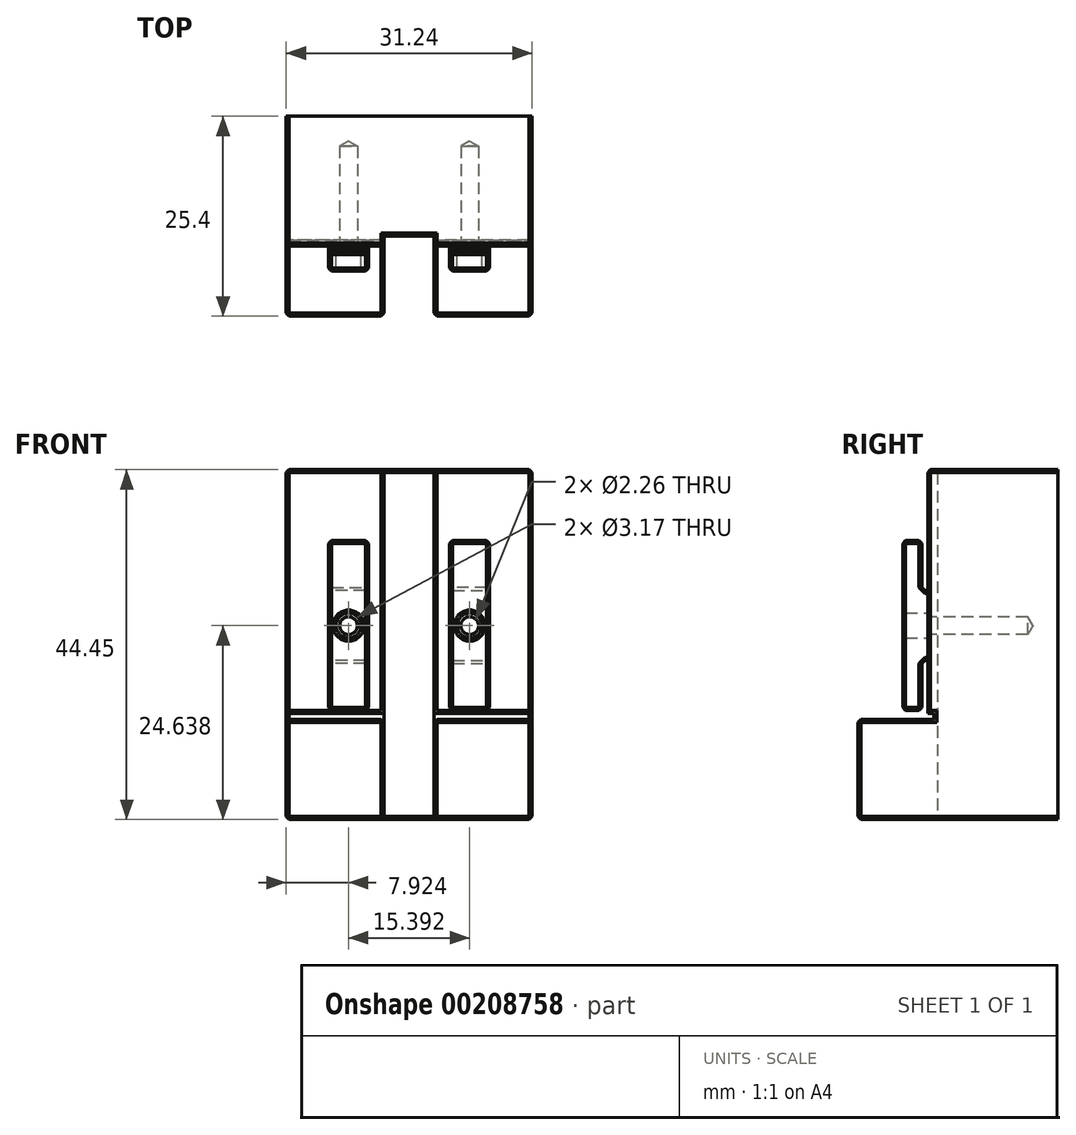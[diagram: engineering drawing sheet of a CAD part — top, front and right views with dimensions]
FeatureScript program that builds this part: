
annotation { "Feature Type Name" : "Feature", "Feature Type Description" : "" }
export const myFeature = defineFeature(function(context is Context, id is Id, definition is map)
    precondition{}
    {
        {
            var Q0;
            Q0=qCreatedBy(makeId("Top.planeOp"),FACE);
            var sketch = newSketch(context, id + "F0", { "sketchPlane" : qUnion([Q0])});
            skLineSegment(sketch, "E0.bottom", {"start": v(15.62, 19.05) * mm, "end": v(3.18, 19.05) * mm});
            skLineSegment(sketch, "E0.top", {"start": v(15.62, -19.05) * mm, "end": v(3.17, -19.05) * mm});
            skLineSegment(sketch, "E0.left", {"start": v(15.62, 19.05) * mm, "end": v(15.62, -19.05) * mm});
            skLineSegment(sketch, "E0.right", {"start": v(-15.62, 19.05) * mm, "end": v(-15.62, -19.05) * mm});
            skPoint(sketch, "E0.middle", {"position": v(0, 0) * mm});
            skLineSegment(sketch, "E1.0", {"start": v(-3.17, 19.05) * mm, "end": v(-3.18, 8.89) * mm});
            skLineSegment(sketch, "E2.0", {"start": v(3.18, 19.05) * mm, "end": v(3.18, 8.89) * mm});
            skLineSegment(sketch, "E3.0", {"start": v(3.18, -8.89) * mm, "end": v(-3.18, -8.89) * mm});
            skLineSegment(sketch, "E4.0", {"start": v(3.18, 8.89) * mm, "end": v(-3.18, 8.89) * mm});
            skLineSegment(sketch, "E5.trimOffspring", {"start": v(-3.18, 19.05) * mm, "end": v(-15.62, 19.05) * mm});
            skLineSegment(sketch, "E6.trimOffspring", {"start": v(-3.18, -8.89) * mm, "end": v(-3.18, -19.05) * mm});
            skLineSegment(sketch, "E7.trimOffspring", {"start": v(3.18, -8.89) * mm, "end": v(3.17, -19.05) * mm});
            skLineSegment(sketch, "E8.trimOffspring", {"start": v(-3.18, -19.05) * mm, "end": v(-15.62, -19.05) * mm});
            skSolve(sketch);
        }
        {
            var Q0;
            Q0=makeQuery(id+"F0.imprint","IMPRINT",FACE,{"disambiguationData":[TD([[makeQuery(id+"F0.imprint","IMPRINT",EDGE,{"derivedFrom":sQuery(id+"F0.wireOp",EDGE,"E0.bottom")}),1.0]])]});
            extrude(context, id + "F1", {"entities" : qUnion([Q0]), "depth" : 44.45 * mm});
        }
        {
            var Q0;
            Q0=makeQuery(id+"F1.opExtrude","CAP_FACE",FACE,{"disambiguationData":[OSD([sQuery(id+"F0.wireOp",EDGE,"E0.bottom"),sQuery(id+"F0.wireOp",EDGE,"E0.top"),sQuery(id+"F0.wireOp",EDGE,"E0.left"),sQuery(id+"F0.wireOp",EDGE,"E0.right"),sQuery(id+"F0.wireOp",EDGE,"E1.0"),sQuery(id+"F0.wireOp",EDGE,"E2.0"),sQuery(id+"F0.wireOp",EDGE,"E3.0"),sQuery(id+"F0.wireOp",EDGE,"E4.0"),sQuery(id+"F0.wireOp",EDGE,"E5.trimOffspring"),sQuery(id+"F0.wireOp",EDGE,"E6.trimOffspring"),sQuery(id+"F0.wireOp",EDGE,"E7.trimOffspring"),sQuery(id+"F0.wireOp",EDGE,"E8.trimOffspring")])],"isStart":false});
            var sketch = newSketch(context, id + "F2", { "sketchPlane" : qUnion([Q0])});
            skLineSegment(sketch, "E9.bottom", {"start": v(-15.62, -19.05) * mm, "end": v(15.62, -19.05) * mm});
            skLineSegment(sketch, "E9.top", {"start": v(-15.62, -10.16) * mm, "end": v(15.62, -10.16) * mm});
            skLineSegment(sketch, "E9.left", {"start": v(-15.62, -19.05) * mm, "end": v(-15.62, -10.16) * mm});
            skLineSegment(sketch, "E9.right", {"start": v(15.62, -19.05) * mm, "end": v(15.62, -10.16) * mm});
            skLineSegment(sketch, "E10.MirrorCS", {"start": v(-15.62, 10.16) * mm, "end": v(15.62, 10.16) * mm});
            skLineSegment(sketch, "E11.MirrorCS", {"start": v(-15.62, 19.05) * mm, "end": v(-15.62, 10.16) * mm});
            skLineSegment(sketch, "E12.MirrorCS", {"start": v(-15.62, 19.05) * mm, "end": v(15.62, 19.05) * mm});
            skLineSegment(sketch, "E13.MirrorCS", {"start": v(15.62, 19.05) * mm, "end": v(15.62, 10.16) * mm});
            skSolve(sketch);
        }
        {
            var Q0;
            {var subQ0=sQuery(id+"F2.wireOp",EDGE,"E9.left");Q0=makeQuery(id+"F2.imprint","IMPRINT",FACE,{"disambiguationData":[TD([[makeQuery(id+"F2.imprint","IMPRINT",EDGE,{"derivedFrom":subQ0}),1.0]])]});}
            var Q1;
            {var subQ0=sQuery(id+"F2.wireOp",EDGE,"E9.right");Q1=makeQuery(id+"F2.imprint","IMPRINT",FACE,{"disambiguationData":[TD([[makeQuery(id+"F2.imprint","IMPRINT",EDGE,{"derivedFrom":subQ0}),-1.0]])]});}
            var Q2;
            {var subQ0=sQuery(id+"F2.wireOp",EDGE,"E13.MirrorCS");Q2=makeQuery(id+"F2.imprint","IMPRINT",FACE,{"disambiguationData":[TD([[makeQuery(id+"F2.imprint","IMPRINT",EDGE,{"derivedFrom":subQ0}),-1.0]])]});}
            var Q3;
            {var subQ0=sQuery(id+"F2.wireOp",EDGE,"E11.MirrorCS");Q3=makeQuery(id+"F2.imprint","IMPRINT",FACE,{"disambiguationData":[TD([[makeQuery(id+"F2.imprint","IMPRINT",EDGE,{"derivedFrom":subQ0}),1.0]])]});}
            extrude(context, id + "F3", {"entities" : qUnion([Q0, Q1, Q2, Q3]), "operationType" : NewBodyOperationType.REMOVE, "oppositeDirection" : true, "depth" : 31.75 * mm});
        }
        {
            var Q0;
            Q0=makeQuery(id+"F1.opExtrude","SWEPT_FACE",FACE,{"disambiguationData":[OSD([sQuery(id+"F0.wireOp",EDGE,"E0.left")])]});
            var sketch = newSketch(context, id + "F4", { "sketchPlane" : qUnion([Q0])});
            skLineSegment(sketch, "E14.bottom", {"start": v(-10.16, 12.7) * mm, "end": v(-9.37, 12.7) * mm});
            skLineSegment(sketch, "E14.top", {"start": v(-10.16, 13.49) * mm, "end": v(-9.37, 13.49) * mm});
            skLineSegment(sketch, "E14.left", {"start": v(-10.16, 12.7) * mm, "end": v(-10.16, 13.49) * mm});
            skLineSegment(sketch, "E14.right", {"start": v(-9.37, 12.7) * mm, "end": v(-9.37, 13.49) * mm});
            skLineSegment(sketch, "E15.MirrorCS", {"start": v(10.16, 13.49) * mm, "end": v(9.37, 13.49) * mm});
            skLineSegment(sketch, "E16.MirrorCS", {"start": v(9.37, 12.7) * mm, "end": v(9.37, 13.49) * mm});
            skLineSegment(sketch, "E17.MirrorCS", {"start": v(10.16, 12.7) * mm, "end": v(9.37, 12.7) * mm});
            skLineSegment(sketch, "E18.MirrorCS", {"start": v(10.16, 12.7) * mm, "end": v(10.16, 13.49) * mm});
            skSolve(sketch);
        }
        {
            var Q0;
            Q0=makeQuery(id+"F4.imprint","IMPRINT",FACE,{"disambiguationData":[TD([[makeQuery(id+"F4.imprint","IMPRINT",EDGE,{"derivedFrom":sQuery(id+"F4.wireOp",EDGE,"E14.bottom")}),1.0]])]});
            var Q1;
            Q1=makeQuery(id+"F4.imprint","IMPRINT",FACE,{"disambiguationData":[TD([[makeQuery(id+"F4.imprint","IMPRINT",EDGE,{"derivedFrom":sQuery(id+"F4.wireOp",EDGE,"E15.MirrorCS")}),1.0]])]});
            extrude(context, id + "F5", {"entities" : qUnion([Q0, Q1]), "operationType" : NewBodyOperationType.REMOVE, "endBound" : BoundingType.THROUGH_ALL, "oppositeDirection" : true, "depth" : 25.4 * mm});
        }
        {
            var Q0;
            {var subQ0=sQuery(id+"F2.wireOp",EDGE,"E10.MirrorCS");Q0=makeQuery(id+"F3.boolean.opBoolean","COPY",FACE,{"derivedFrom":makeQuery(id+"F3.opExtrude","SWEPT_FACE",FACE,{"disambiguationData":[OSD([subQ0]),TDD([makeQuery(id+"F2.imprint","IMPRINT",EDGE,{"disambiguationData":[TD([[makeQuery(id+"F2.imprint","INTERSECT",VERTEX,{"derivedFrom":[makeQuery(id+"F1.opExtrude","CAP_EDGE",EDGE,{"disambiguationData":[OSD([sQuery(id+"F0.wireOp",EDGE,"E2.0")])],"isStart":false}),subQ0]}),-1.0]])],"derivedFrom":subQ0})])]})});}
            var Q1;
            {var subQ0=sQuery(id+"F2.wireOp",EDGE,"E10.MirrorCS");Q1=makeQuery(id+"F3.boolean.opBoolean","COPY",FACE,{"derivedFrom":makeQuery(id+"F3.opExtrude","SWEPT_FACE",FACE,{"disambiguationData":[OSD([subQ0]),TDD([makeQuery(id+"F2.imprint","IMPRINT",EDGE,{"disambiguationData":[TD([[makeQuery(id+"F2.imprint","INTERSECT",VERTEX,{"derivedFrom":[makeQuery(id+"F1.opExtrude","CAP_EDGE",EDGE,{"disambiguationData":[OSD([sQuery(id+"F0.wireOp",EDGE,"E1.0")])],"isStart":false}),subQ0]}),1.0]])],"derivedFrom":subQ0})])]})});}
            var Q2;
            Q2=makeQuery(id+"F1.opExtrude","SWEPT_FACE",FACE,{"disambiguationData":[OSD([sQuery(id+"F0.wireOp",EDGE,"E5.trimOffspring")])]});
            var Q3;
            Q3=makeQuery(id+"F1.opExtrude","SWEPT_FACE",FACE,{"disambiguationData":[OSD([sQuery(id+"F0.wireOp",EDGE,"E0.bottom")])]});
            var Q4;
            Q4=makeQuery(id+"F1.opExtrude","SWEPT_FACE",FACE,{"disambiguationData":[OSD([sQuery(id+"F0.wireOp",EDGE,"E0.right")])]});
            var Q5;
            {var subQ0=sQuery(id+"F2.wireOp",EDGE,"E9.top");Q5=makeQuery(id+"F3.boolean.opBoolean","COPY",FACE,{"derivedFrom":makeQuery(id+"F3.opExtrude","SWEPT_FACE",FACE,{"disambiguationData":[OSD([subQ0]),TDD([makeQuery(id+"F2.imprint","IMPRINT",EDGE,{"disambiguationData":[TD([[makeQuery(id+"F2.imprint","INTERSECT",VERTEX,{"derivedFrom":[makeQuery(id+"F1.opExtrude","CAP_EDGE",EDGE,{"disambiguationData":[OSD([sQuery(id+"F0.wireOp",EDGE,"E7.trimOffspring")])],"isStart":false}),subQ0]}),-1.0]])],"derivedFrom":subQ0})])]})});}
            var Q6;
            Q6=makeQuery(id+"F1.opExtrude","SWEPT_FACE",FACE,{"disambiguationData":[OSD([sQuery(id+"F0.wireOp",EDGE,"E0.top")])]});
            var Q7;
            Q7=makeQuery(id+"F1.opExtrude","SWEPT_FACE",FACE,{"disambiguationData":[OSD([sQuery(id+"F0.wireOp",EDGE,"E8.trimOffspring")])]});
            var Q8;
            Q8=makeQuery(id+"F1.opExtrude","CAP_FACE",FACE,{"disambiguationData":[OSD([sQuery(id+"F0.wireOp",EDGE,"E0.bottom"),sQuery(id+"F0.wireOp",EDGE,"E0.top"),sQuery(id+"F0.wireOp",EDGE,"E0.left"),sQuery(id+"F0.wireOp",EDGE,"E0.right"),sQuery(id+"F0.wireOp",EDGE,"E1.0"),sQuery(id+"F0.wireOp",EDGE,"E2.0"),sQuery(id+"F0.wireOp",EDGE,"E3.0"),sQuery(id+"F0.wireOp",EDGE,"E4.0"),sQuery(id+"F0.wireOp",EDGE,"E5.trimOffspring"),sQuery(id+"F0.wireOp",EDGE,"E6.trimOffspring"),sQuery(id+"F0.wireOp",EDGE,"E7.trimOffspring"),sQuery(id+"F0.wireOp",EDGE,"E8.trimOffspring")])],"isStart":true});
            var Q9;
            Q9=makeQuery(id+"F1.opExtrude","CAP_FACE",FACE,{"disambiguationData":[OSD([sQuery(id+"F0.wireOp",EDGE,"E0.bottom"),sQuery(id+"F0.wireOp",EDGE,"E0.top"),sQuery(id+"F0.wireOp",EDGE,"E0.left"),sQuery(id+"F0.wireOp",EDGE,"E0.right"),sQuery(id+"F0.wireOp",EDGE,"E1.0"),sQuery(id+"F0.wireOp",EDGE,"E2.0"),sQuery(id+"F0.wireOp",EDGE,"E3.0"),sQuery(id+"F0.wireOp",EDGE,"E4.0"),sQuery(id+"F0.wireOp",EDGE,"E5.trimOffspring"),sQuery(id+"F0.wireOp",EDGE,"E6.trimOffspring"),sQuery(id+"F0.wireOp",EDGE,"E7.trimOffspring"),sQuery(id+"F0.wireOp",EDGE,"E8.trimOffspring")])],"isStart":false});
            var Q10;
            Q10=makeQuery(id+"F5.boolean.opBoolean","INTERSECT",EDGE,{"derivedFrom":[makeQuery(id+"F1.opExtrude","SWEPT_FACE",FACE,{"disambiguationData":[OSD([sQuery(id+"F0.wireOp",EDGE,"E6.trimOffspring")])]}),makeQuery(id+"F5.opExtrude","SWEPT_FACE",FACE,{"disambiguationData":[OSD([sQuery(id+"F4.wireOp",EDGE,"E14.bottom")])]})]});
            var Q11;
            Q11=makeQuery(id+"F5.boolean.opBoolean","INTERSECT",EDGE,{"derivedFrom":[makeQuery(id+"F1.opExtrude","SWEPT_FACE",FACE,{"disambiguationData":[OSD([sQuery(id+"F0.wireOp",EDGE,"E7.trimOffspring")])]}),makeQuery(id+"F5.opExtrude","SWEPT_FACE",FACE,{"disambiguationData":[OSD([sQuery(id+"F4.wireOp",EDGE,"E14.bottom")])]})]});
            var Q12;
            Q12=makeQuery(id+"F5.boolean.opBoolean","INTERSECT",EDGE,{"derivedFrom":[makeQuery(id+"F1.opExtrude","SWEPT_FACE",FACE,{"disambiguationData":[OSD([sQuery(id+"F0.wireOp",EDGE,"E2.0")])]}),makeQuery(id+"F5.opExtrude","SWEPT_FACE",FACE,{"disambiguationData":[OSD([sQuery(id+"F4.wireOp",EDGE,"E17.MirrorCS")])]})]});
            var Q13;
            Q13=makeQuery(id+"F5.boolean.opBoolean","INTERSECT",EDGE,{"derivedFrom":[makeQuery(id+"F1.opExtrude","SWEPT_FACE",FACE,{"disambiguationData":[OSD([sQuery(id+"F0.wireOp",EDGE,"E1.0")])]}),makeQuery(id+"F5.opExtrude","SWEPT_FACE",FACE,{"disambiguationData":[OSD([sQuery(id+"F4.wireOp",EDGE,"E17.MirrorCS")])]})]});
            var Q14;
            Q14=makeQuery(id+"F5.boolean.opBoolean","MERGE",EDGE,{"derivedFrom":[makeQuery(id+"F3.boolean.opBoolean","COPY",EDGE,{"derivedFrom":makeQuery(id+"F3.opExtrude","CAP_EDGE",EDGE,{"disambiguationData":[OSD([sQuery(id+"F2.wireOp",EDGE,"E9.right")])],"isStart":false})}),makeQuery(id+"F5.opExtrude","CAP_EDGE",EDGE,{"disambiguationData":[OSD([sQuery(id+"F4.wireOp",EDGE,"E14.bottom")])],"isStart":true})]});
            var Q15;
            Q15=makeQuery(id+"F3.boolean.opBoolean","COPY",EDGE,{"derivedFrom":makeQuery(id+"F3.opExtrude","SWEPT_EDGE",EDGE,{"disambiguationData":[OSD([sQuery(id+"F0.wireOp",EDGE,"E6.trimOffspring"),sQuery(id+"F2.wireOp",EDGE,"E9.top")])]})});
            var Q16;
            Q16=makeQuery(id+"F5.boolean.opBoolean","MERGE",EDGE,{"derivedFrom":[makeQuery(id+"F3.boolean.opBoolean","COPY",EDGE,{"derivedFrom":makeQuery(id+"F3.opExtrude","CAP_EDGE",EDGE,{"disambiguationData":[OSD([sQuery(id+"F2.wireOp",EDGE,"E13.MirrorCS")])],"isStart":false})}),makeQuery(id+"F5.opExtrude","CAP_EDGE",EDGE,{"disambiguationData":[OSD([sQuery(id+"F4.wireOp",EDGE,"E17.MirrorCS")])],"isStart":true})]});
            chamfer(context, id + "F6", {"entities" : qUnion([Q0, Q1, Q2, Q3, Q4, Q5, Q6, Q7, Q8, Q9, Q10, Q11, Q12, Q13, Q14, Q15, Q16]), "width" : 0.38 * mm, "tangentPropagation" : true});
        }
        {
            var Q0;
            {var subQ0=sQuery(id+"F2.wireOp",EDGE,"E9.top");Q0=makeQuery(id+"F3.boolean.opBoolean","COPY",FACE,{"derivedFrom":makeQuery(id+"F3.opExtrude","SWEPT_FACE",FACE,{"disambiguationData":[OSD([subQ0]),TDD([makeQuery(id+"F2.imprint","IMPRINT",EDGE,{"disambiguationData":[TD([[makeQuery(id+"F2.imprint","INTERSECT",VERTEX,{"derivedFrom":[makeQuery(id+"F1.opExtrude","CAP_EDGE",EDGE,{"disambiguationData":[OSD([sQuery(id+"F0.wireOp",EDGE,"E7.trimOffspring")])],"isStart":false}),subQ0]}),-1.0]])],"derivedFrom":subQ0})])]})});}
            var sketch = newSketch(context, id + "F7", { "sketchPlane" : qUnion([Q0])});
            skCircle(sketch, "E19", {"center": v(7.7, 24.64) * mm, "radius": 1.42 * mm});
            skSolve(sketch);
        }
        {
            var Q0;
            Q0=sQuery(id+"F7.wireOp",VERTEX,"E19.center");
            var Q1;
            Q1=makeQuery(id+"F1.opExtrude","SWEPT_BODY",BODY,{"disambiguationData":[OSD([sQuery(id+"F0.wireOp",EDGE,"E0.bottom"),sQuery(id+"F0.wireOp",EDGE,"E0.top"),sQuery(id+"F0.wireOp",EDGE,"E0.left"),sQuery(id+"F0.wireOp",EDGE,"E0.right"),sQuery(id+"F0.wireOp",EDGE,"E1.0"),sQuery(id+"F0.wireOp",EDGE,"E2.0"),sQuery(id+"F0.wireOp",EDGE,"E3.0"),sQuery(id+"F0.wireOp",EDGE,"E4.0"),sQuery(id+"F0.wireOp",EDGE,"E5.trimOffspring"),sQuery(id+"F0.wireOp",EDGE,"E6.trimOffspring"),sQuery(id+"F0.wireOp",EDGE,"E7.trimOffspring"),sQuery(id+"F0.wireOp",EDGE,"E8.trimOffspring")])]});
            hole(context, id + "F8", {"style" : HoleStyle.SIMPLE, "endStyle" : HoleEndStyle.BLIND, "standardTappedOrClearance" : lookupTablePath({ "standard" : "ANSI", "engagement" : "75%", "pitch" : "40 tpi", "size" : "#4", "type" : "Tapped" }), "standardBlindInLast" : lookupTablePath({ "standard" : "ANSI", "engagement" : "75%", "pitch" : "40 tpi", "size" : "#4", "type" : "Tapped" }), "holeDiameter" : 2.26 * mm, "showTappedDepth" : true, "holeDepth" : 12.7 * mm, "tappedDepth" : 10.8 * mm, "tapClearance" : 3, "startFromSketch" : true, "locations" : qUnion([Q0]), "scope" : qUnion([Q1]), "majorDiameter" : 2.84 * mm});
        }
        {
            var Q0;
            {var subQ0=sQuery(id+"F2.wireOp",EDGE,"E9.top");Q0=makeQuery(id+"F3.boolean.opBoolean","COPY",FACE,{"derivedFrom":makeQuery(id+"F3.opExtrude","SWEPT_FACE",FACE,{"disambiguationData":[OSD([subQ0]),TDD([makeQuery(id+"F2.imprint","IMPRINT",EDGE,{"disambiguationData":[TD([[makeQuery(id+"F2.imprint","INTERSECT",VERTEX,{"derivedFrom":[makeQuery(id+"F1.opExtrude","CAP_EDGE",EDGE,{"disambiguationData":[OSD([sQuery(id+"F0.wireOp",EDGE,"E7.trimOffspring")])],"isStart":false}),subQ0]}),-1.0]])],"derivedFrom":subQ0})])]})});}
            var sketch = newSketch(context, id + "F9", { "sketchPlane" : qUnion([Q0])});
            skLineSegment(sketch, "E20.bottom", {"start": v(10.24, 35.43) * mm, "end": v(5.16, 35.43) * mm});
            skLineSegment(sketch, "E20.top", {"start": v(10.24, 13.84) * mm, "end": v(5.16, 13.84) * mm});
            skLineSegment(sketch, "E20.left", {"start": v(10.24, 35.43) * mm, "end": v(10.24, 13.84) * mm});
            skLineSegment(sketch, "E20.right", {"start": v(5.16, 35.43) * mm, "end": v(5.16, 13.84) * mm});
            skPoint(sketch, "E20.middle", {"position": v(7.7, 24.64) * mm});
            skCircle(sketch, "E21", {"center": v(7.7, 24.64) * mm, "radius": 1.59 * mm});
            skSolve(sketch);
        }
        {
            var Q0;
            {var subQ10=sQuery(id+"F9.wireOp",EDGE,"E20.bottom");Q0=makeQuery(id+"F9.imprint","IMPRINT",FACE,{"disambiguationData":[TD([[makeQuery(id+"F9.imprint","IMPRINT",EDGE,{"derivedFrom":subQ10}),1.0]])]});}
            extrude(context, id + "F10", {"entities" : qUnion([Q0]), "depth" : 3.17 * mm});
        }
        {
            var Q0;
            Q0=makeQuery(id+"F10.opExtrude","SWEPT_FACE",FACE,{"disambiguationData":[OSD([sQuery(id+"F9.wireOp",EDGE,"E20.left")])]});
            var sketch = newSketch(context, id + "F11", { "sketchPlane" : qUnion([Q0])});
            skLineSegment(sketch, "E22.bottom", {"start": v(-10.16, 35.43) * mm, "end": v(-10.87, 35.43) * mm});
            skLineSegment(sketch, "E22.top", {"start": v(-10.16, 29.08) * mm, "end": v(-10.87, 29.08) * mm});
            skLineSegment(sketch, "E22.left", {"start": v(-10.16, 35.43) * mm, "end": v(-10.16, 29.08) * mm});
            skLineSegment(sketch, "E22.right", {"start": v(-10.87, 35.43) * mm, "end": v(-10.87, 29.08) * mm});
            skLineSegment(sketch, "E23.bottom", {"start": v(-10.16, 13.87) * mm, "end": v(-10.87, 13.87) * mm});
            skLineSegment(sketch, "E23.top", {"start": v(-10.16, 20.22) * mm, "end": v(-10.87, 20.22) * mm});
            skLineSegment(sketch, "E23.left", {"start": v(-10.16, 13.87) * mm, "end": v(-10.16, 20.22) * mm});
            skLineSegment(sketch, "E23.right", {"start": v(-10.87, 13.87) * mm, "end": v(-10.87, 20.22) * mm});
            skSolve(sketch);
        }
        {
            var Q0;
            Q0=makeQuery(id+"F11.imprint","IMPRINT",FACE,{"disambiguationData":[TD([[makeQuery(id+"F11.imprint","IMPRINT",EDGE,{"derivedFrom":sQuery(id+"F11.wireOp",EDGE,"E23.bottom")}),1.0]])]});
            var Q1;
            Q1=makeQuery(id+"F11.imprint","IMPRINT",FACE,{"disambiguationData":[TD([[makeQuery(id+"F11.imprint","IMPRINT",EDGE,{"derivedFrom":sQuery(id+"F11.wireOp",EDGE,"E22.bottom")}),-1.0]])]});
            extrude(context, id + "F12", {"entities" : qUnion([Q0, Q1]), "operationType" : NewBodyOperationType.REMOVE, "endBound" : BoundingType.THROUGH_ALL, "oppositeDirection" : true, "depth" : 12.7 * mm});
        }
        {
            var Q0;
            Q0=makeQuery(id+"F10.opExtrude","CAP_FACE",FACE,{"disambiguationData":[OSD([sQuery(id+"F0.wireOp",EDGE,"E0.left"),sQuery(id+"F2.wireOp",EDGE,"E9.top"),sQuery(id+"F2.wireOp",EDGE,"E9.right"),sQuery(id+"F4.wireOp",EDGE,"E14.top"),sQuery(id+"F4.wireOp",EDGE,"E14.left"),sQuery(id+"F9.wireOp",EDGE,"E20.bottom"),sQuery(id+"F9.wireOp",EDGE,"E20.left"),sQuery(id+"F9.wireOp",EDGE,"E20.right"),sQuery(id+"F9.wireOp",EDGE,"E21")])],"isStart":false});
            var Q1;
            Q1=makeQuery(id+"F10.opExtrude","SWEPT_FACE",FACE,{"disambiguationData":[OSD([sQuery(id+"F9.wireOp",EDGE,"E20.bottom")])]});
            var Q2;
            Q2=makeQuery(id+"F10.opExtrude","SWEPT_FACE",FACE,{"disambiguationData":[OSD([sQuery(id+"F0.wireOp",EDGE,"E0.left"),sQuery(id+"F2.wireOp",EDGE,"E9.top"),sQuery(id+"F2.wireOp",EDGE,"E9.right"),sQuery(id+"F4.wireOp",EDGE,"E14.top"),sQuery(id+"F4.wireOp",EDGE,"E14.left")])]});
            var Q3;
            Q3=makeQuery(id+"F12.boolean.opBoolean","COPY",FACE,{"derivedFrom":makeQuery(id+"F12.opExtrude","SWEPT_FACE",FACE,{"disambiguationData":[OSD([sQuery(id+"F11.wireOp",EDGE,"E23.right")])]})});
            var Q4;
            Q4=makeQuery(id+"F12.boolean.opBoolean","COPY",FACE,{"derivedFrom":makeQuery(id+"F12.opExtrude","SWEPT_FACE",FACE,{"disambiguationData":[OSD([sQuery(id+"F11.wireOp",EDGE,"E22.right")])]})});
            chamfer(context, id + "F13", {"entities" : qUnion([Q0, Q1, Q2, Q3, Q4]), "width" : 0.38 * mm, "tangentPropagation" : true});
        }
        {
            var Q0;
            Q0=makeQuery(id+"F1.opExtrude","CAP_FACE",FACE,{"disambiguationData":[OSD([sQuery(id+"F0.wireOp",EDGE,"E0.bottom"),sQuery(id+"F0.wireOp",EDGE,"E0.top"),sQuery(id+"F0.wireOp",EDGE,"E0.left"),sQuery(id+"F0.wireOp",EDGE,"E0.right"),sQuery(id+"F0.wireOp",EDGE,"E1.0"),sQuery(id+"F0.wireOp",EDGE,"E2.0"),sQuery(id+"F0.wireOp",EDGE,"E3.0"),sQuery(id+"F0.wireOp",EDGE,"E4.0"),sQuery(id+"F0.wireOp",EDGE,"E5.trimOffspring"),sQuery(id+"F0.wireOp",EDGE,"E6.trimOffspring"),sQuery(id+"F0.wireOp",EDGE,"E7.trimOffspring"),sQuery(id+"F0.wireOp",EDGE,"E8.trimOffspring")])],"isStart":true});
            var sketch = newSketch(context, id + "F14", { "sketchPlane" : qUnion([Q0])});
            skLineSegment(sketch, "E24", {"start": v(20.64, -6.35) * mm, "end": v(-21.81, -6.35) * mm});
            skLineSegment(sketch, "E25", {"start": v(-21.81, -6.35) * mm, "end": v(-21.81, -30) * mm});
            skLineSegment(sketch, "E26", {"start": v(-21.81, -30) * mm, "end": v(20.64, -30) * mm});
            skLineSegment(sketch, "E27", {"start": v(20.64, -30) * mm, "end": v(20.64, -6.35) * mm});
            skSolve(sketch);
        }
        {
            var Q0;
            Q0 = qSketchRegion(id + "F14", true);
            extrude(context, id + "F15", {"entities" : qUnion([Q0]), "operationType" : NewBodyOperationType.REMOVE, "endBound" : BoundingType.THROUGH_ALL, "oppositeDirection" : true, "depth" : 25.4 * mm});
        }
        {
            var Q0;
            Q0=makeQuery(id+"F10.opExtrude","SWEPT_BODY",BODY,{"disambiguationData":[OSD([sQuery(id+"F0.wireOp",EDGE,"E0.left"),sQuery(id+"F2.wireOp",EDGE,"E9.top"),sQuery(id+"F2.wireOp",EDGE,"E9.right"),sQuery(id+"F4.wireOp",EDGE,"E14.top"),sQuery(id+"F4.wireOp",EDGE,"E14.left"),sQuery(id+"F9.wireOp",EDGE,"E20.bottom"),sQuery(id+"F9.wireOp",EDGE,"E20.left"),sQuery(id+"F9.wireOp",EDGE,"E20.right"),sQuery(id+"F9.wireOp",EDGE,"E21")])]});
            var Q1;
            Q1=makeQuery(id+"F1.opExtrude","SWEPT_BODY",BODY,{"disambiguationData":[OSD([sQuery(id+"F0.wireOp",EDGE,"E0.bottom"),sQuery(id+"F0.wireOp",EDGE,"E0.top"),sQuery(id+"F0.wireOp",EDGE,"E0.left"),sQuery(id+"F0.wireOp",EDGE,"E0.right"),sQuery(id+"F0.wireOp",EDGE,"E1.0"),sQuery(id+"F0.wireOp",EDGE,"E2.0"),sQuery(id+"F0.wireOp",EDGE,"E3.0"),sQuery(id+"F0.wireOp",EDGE,"E4.0"),sQuery(id+"F0.wireOp",EDGE,"E5.trimOffspring"),sQuery(id+"F0.wireOp",EDGE,"E6.trimOffspring"),sQuery(id+"F0.wireOp",EDGE,"E7.trimOffspring"),sQuery(id+"F0.wireOp",EDGE,"E8.trimOffspring")])]});
            var Q2;
            Q2=qCreatedBy(makeId("Right.planeOp"),FACE);
            mirror(context, id + "F16", {"entities" : qUnion([Q0, Q1]), "mirrorPlane" : qUnion([Q2])});
        }
    });
